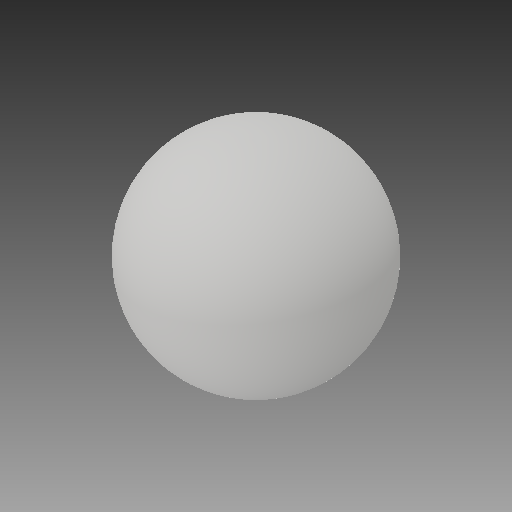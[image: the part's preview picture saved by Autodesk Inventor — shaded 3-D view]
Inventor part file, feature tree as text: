
AUTODESK INVENTOR PART (.ipt)
format: ipt  version: 2018 (Build 220112000, 112)  size: 118,784 bytes
history: native  units: in
note: dims shown in document units (in); Inventor stores cm internally (conversion verified against a paired STEP export)
features: revolve x1, sketch x1
ambient origin geometry x8: Origin, YZ Plane, XZ Plane, XY Plane, X Axis, Y Axis, Z Axis, Center Point
bodies: Solid1 (feature_tree)
feature tree (2):
  revolve  "Revolution1"  Angle=90.0deg
  sketch  "Sketch1"  dims[d0=0.625in d1=90.0deg]
